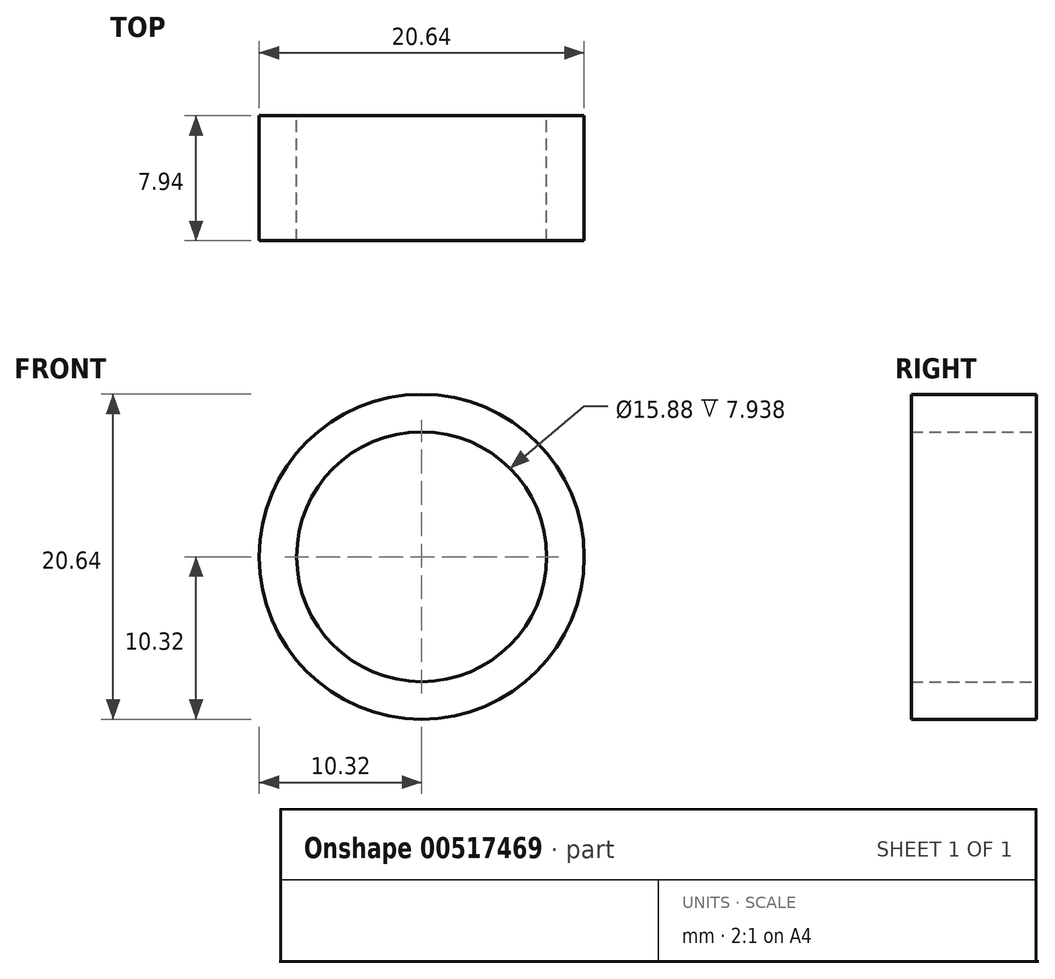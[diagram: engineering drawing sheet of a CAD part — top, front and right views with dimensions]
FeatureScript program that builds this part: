
annotation { "Feature Type Name" : "Feature", "Feature Type Description" : "" }
export const myFeature = defineFeature(function(context is Context, id is Id, definition is map)
    precondition{}
    {
        {
            var Q0;
            Q0=qCreatedBy(makeId("Front.planeOp"),FACE);
            var sketch = newSketch(context, id + "F0", { "sketchPlane" : qUnion([Q0])});
            skCircle(sketch, "E0", {"center": v(0, 0) * mm, "radius": 10.32 * mm});
            skCircle(sketch, "E1", {"center": v(0, 0) * mm, "radius": 7.94 * mm});
            skSolve(sketch);
        }
        {
            var Q0;
            Q0 = qSketchRegion(id + "F0", true);
            extrude(context, id + "F1", {"entities" : qUnion([Q0]), "depth" : 7.94 * mm, "offsetDistance" : 25.4 * mm});
        }
    });
